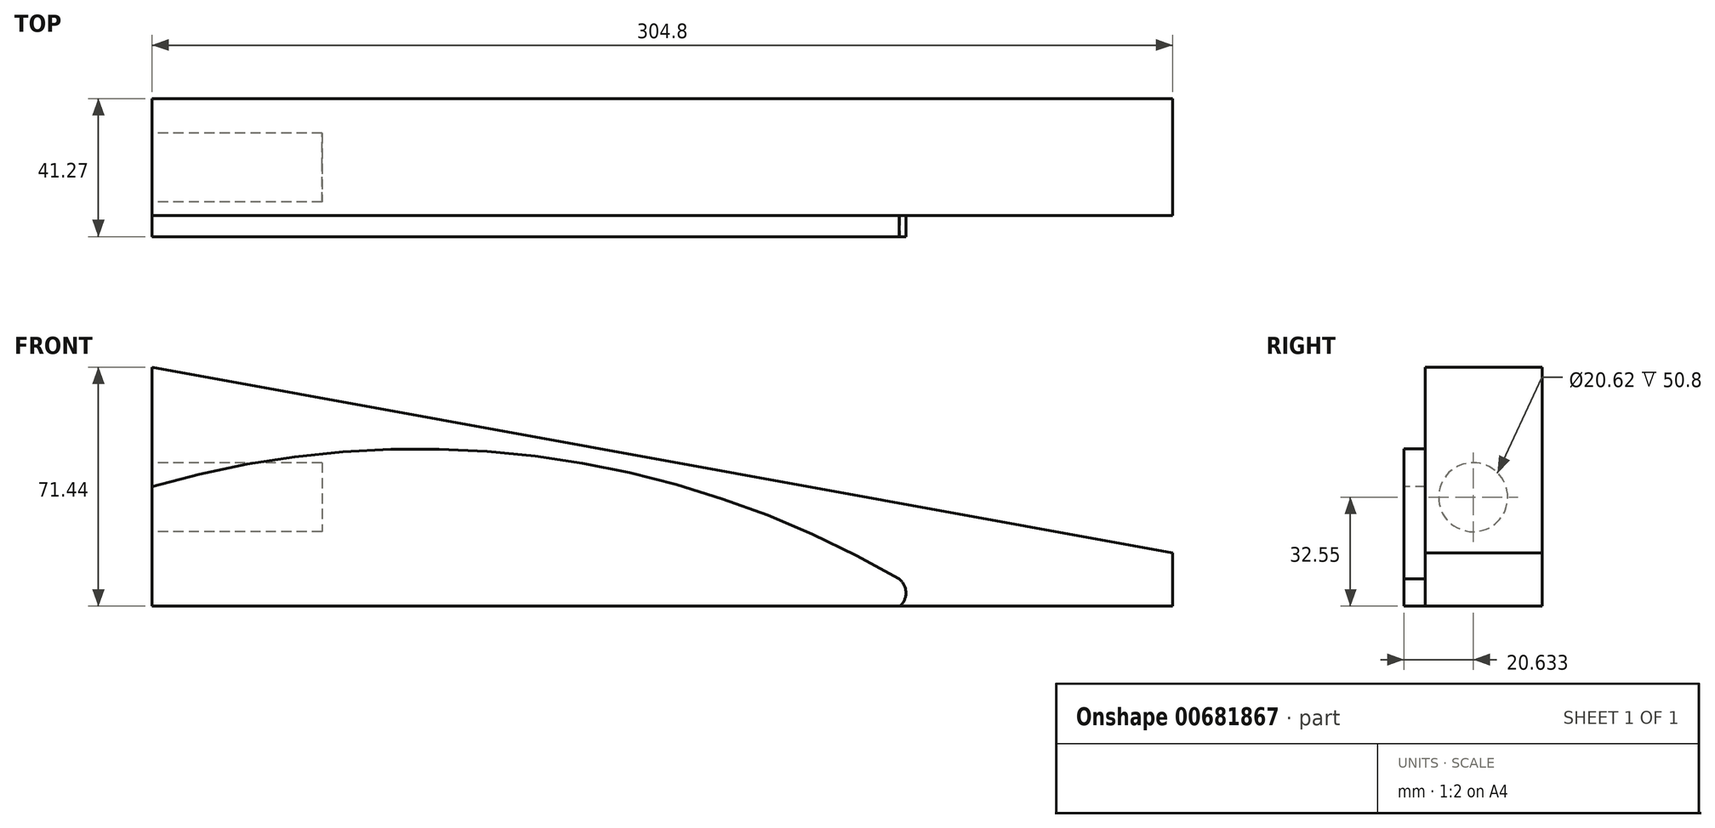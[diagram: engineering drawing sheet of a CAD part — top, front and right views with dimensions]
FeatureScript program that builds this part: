
annotation { "Feature Type Name" : "Feature", "Feature Type Description" : "" }
export const myFeature = defineFeature(function(context is Context, id is Id, definition is map)
    precondition{}
    {
        {
            var Q0;
            Q0=qCreatedBy(makeId("Front.planeOp"),FACE);
            var sketch = newSketch(context, id + "F0", { "sketchPlane" : qUnion([Q0])});
            skLineSegment(sketch, "E0", {"start": v(0, 0) * mm, "end": v(0, 71.44) * mm});
            skLineSegment(sketch, "E1", {"start": v(0, 0) * mm, "end": v(304.8, 0) * mm});
            skLineSegment(sketch, "E2", {"start": v(304.8, 0) * mm, "end": v(304.8, 15.88) * mm});
            skLineSegment(sketch, "E3", {"start": v(0, 71.44) * mm, "end": v(304.8, 15.88) * mm});
            skSolve(sketch);
        }
        {
            var Q0;
            Q0=makeQuery(id+"F0.imprint","IMPRINT",FACE,{"disambiguationData":[TD([[makeQuery(id+"F0.imprint","IMPRINT",EDGE,{"derivedFrom":sQuery(id+"F0.wireOp",EDGE,"E0")}),-1.0]])]});
            extrude(context, id + "F1", {"entities" : qUnion([Q0]), "depth" : 41.27 * mm, "offsetDistance" : 25.4 * mm});
        }
        {
            var Q0;
            Q0=makeQuery(id+"F1.opExtrude","SWEPT_FACE",FACE,{"disambiguationData":[OSD([sQuery(id+"F0.wireOp",EDGE,"E0")])]});
            var sketch = newSketch(context, id + "F2", { "sketchPlane" : qUnion([Q0])});
            skPoint(sketch, "E4.endSnap0", {"position": v(20.64, 71.44) * mm});
            skCircle(sketch, "E5", {"center": v(20.64, 32.55) * mm, "radius": 10.31 * mm});
            skSolve(sketch);
        }
        {
            var Q0;
            Q0=makeQuery(id+"F2.imprint","IMPRINT",FACE,{"disambiguationData":[TD([[makeQuery(id+"F2.imprint","IMPRINT",EDGE,{"derivedFrom":sQuery(id+"F2.wireOp",EDGE,"E5")}),1.0]])]});
            extrude(context, id + "F3", {"entities" : qUnion([Q0]), "operationType" : NewBodyOperationType.REMOVE, "oppositeDirection" : true, "depth" : 50.8 * mm, "offsetDistance" : 25.4 * mm});
        }
        {
            var Q0;
            Q0=makeQuery(id+"F1.opExtrude","CAP_FACE",FACE,{"disambiguationData":[OSD([sQuery(id+"F0.wireOp",EDGE,"E0"),sQuery(id+"F0.wireOp",EDGE,"E1"),sQuery(id+"F0.wireOp",EDGE,"E2"),sQuery(id+"F0.wireOp",EDGE,"E3")])],"isStart":false});
            var sketch = newSketch(context, id + "F4", { "sketchPlane" : qUnion([Q0])});
            skLineSegment(sketch, "E6", {"start": v(0, 35.72) * mm, "end": v(0, 71.44) * mm});
            skLineSegment(sketch, "E7", {"start": v(304.8, 7.94) * mm, "end": v(304.8, 15.87) * mm});
            skArc(sketch, "E8", {"start": v(223.1, 8.13) * mm, "mid": v(114.38, 44.81) * mm, "end": v(0, 35.72) * mm});
            skArc(sketch, "E9", {"start": v(223.4, 0) * mm, "mid": v(225.15, 4.14) * mm, "end": v(223.1, 8.13) * mm});
            skPoint(sketch, "E10.orphan", {"position": v(236.22, 0) * mm});
            skSolve(sketch);
        }
        {
            var Q0;
            Q0=makeQuery(id+"F4.imprint","IMPRINT",FACE,{"disambiguationData":[TD([[makeQuery(id+"F4.imprint","IMPRINT",EDGE,{"derivedFrom":sQuery(id+"F4.wireOp",EDGE,"E6")}),-1.0]])]});
            extrude(context, id + "F5", {"entities" : qUnion([Q0]), "operationType" : NewBodyOperationType.REMOVE, "oppositeDirection" : true, "depth" : 6.35 * mm, "offsetDistance" : 25.4 * mm});
        }
        {
            var Q0;
            Q0=qCreatedBy(makeId("Front.planeOp"),FACE);
            cPlane(context, id + "F6", {"entities" : qUnion([Q0]), "cplaneType" : CPlaneType.OFFSET, "offset" : 20.64 * mm, "width" : 152.4 * mm, "height" : 152.4 * mm});
        }
    });
